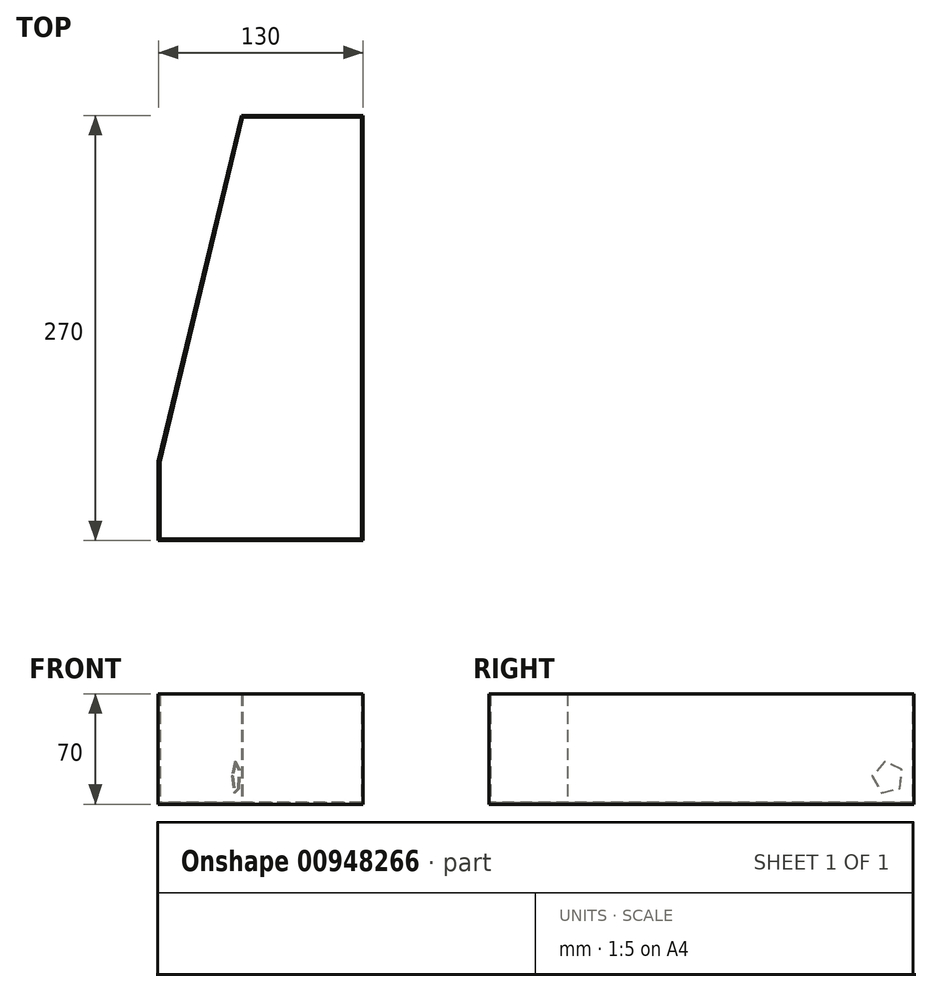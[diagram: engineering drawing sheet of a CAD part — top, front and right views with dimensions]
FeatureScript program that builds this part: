
annotation { "Feature Type Name" : "Feature", "Feature Type Description" : "" }
export const myFeature = defineFeature(function(context is Context, id is Id, definition is map)
    precondition{}
    {
        {
            var Q0;
            Q0=qCreatedBy(makeId("Top.planeOp"),FACE);
            var sketch = newSketch(context, id + "F0", { "sketchPlane" : qUnion([Q0])});
            skLineSegment(sketch, "E0", {"start": v(-26.67, 204.09) * mm, "end": v(50.48, 204.09) * mm});
            skLineSegment(sketch, "E1", {"start": v(50.48, 204.09) * mm, "end": v(50.48, -65.91) * mm});
            skLineSegment(sketch, "E2", {"start": v(50.48, -65.91) * mm, "end": v(-79.52, -65.91) * mm});
            skLineSegment(sketch, "E3", {"start": v(-79.52, -65.91) * mm, "end": v(-79.52, -15.91) * mm});
            skLineSegment(sketch, "E4", {"start": v(-79.52, -15.91) * mm, "end": v(-26.67, 204.09) * mm});
            skSolve(sketch);
        }
        {
            var Q0;
            Q0=makeQuery(id+"F0.imprint","IMPRINT",FACE,{"disambiguationData":[TD([[makeQuery(id+"F0.imprint","IMPRINT",EDGE,{"derivedFrom":sQuery(id+"F0.wireOp",EDGE,"E0")}),-1.0]])]});
            extrude(context, id + "F1", {"entities" : qUnion([Q0]), "depth" : 70 * mm, "offsetDistance" : 25 * mm});
        }
        {
            var Q0;
            Q0=makeQuery(id+"F1.opExtrude","CAP_FACE",FACE,{"disambiguationData":[OSD([sQuery(id+"F0.wireOp",EDGE,"E0"),sQuery(id+"F0.wireOp",EDGE,"E1"),sQuery(id+"F0.wireOp",EDGE,"E2"),sQuery(id+"F0.wireOp",EDGE,"E3"),sQuery(id+"F0.wireOp",EDGE,"E4")])],"isStart":false});
            shell(context, id + "F2", {"entities" : qUnion([Q0]), "thickness" : 1 * mm});
        }
        {
            var Q0;
            Q0=makeQuery(id+"F1.opExtrude","SWEPT_FACE",FACE,{"disambiguationData":[OSD([sQuery(id+"F0.wireOp",EDGE,"E4")])]});
            var sketch = newSketch(context, id + "F3", { "sketchPlane" : qUnion([Q0])});
            skLineSegment(sketch, "E5.0", {"start": v(-173.11, 26.93) * mm, "end": v(-165, 17.79) * mm});
            skLineSegment(sketch, "E5.1", {"start": v(-165, 17.79) * mm, "end": v(-171.2, 7.26) * mm});
            skLineSegment(sketch, "E5.2", {"start": v(-171.2, 7.26) * mm, "end": v(-183.13, 9.89) * mm});
            skLineSegment(sketch, "E5.3", {"start": v(-183.13, 9.89) * mm, "end": v(-184.31, 22.05) * mm});
            skLineSegment(sketch, "E5.4", {"start": v(-184.31, 22.05) * mm, "end": v(-173.11, 26.93) * mm});
            skSolve(sketch);
        }
        {
            var Q0;
            Q0=makeQuery(id+"F3.imprint","IMPRINT",FACE,{"disambiguationData":[TD([[makeQuery(id+"F3.imprint","IMPRINT",EDGE,{"derivedFrom":sQuery(id+"F3.wireOp",EDGE,"E5.0")}),-1.0]])]});
            extrude(context, id + "F4", {"entities" : qUnion([Q0]), "operationType" : NewBodyOperationType.REMOVE, "oppositeDirection" : true, "depth" : 4 * mm, "offsetDistance" : 25 * mm});
        }
    });
